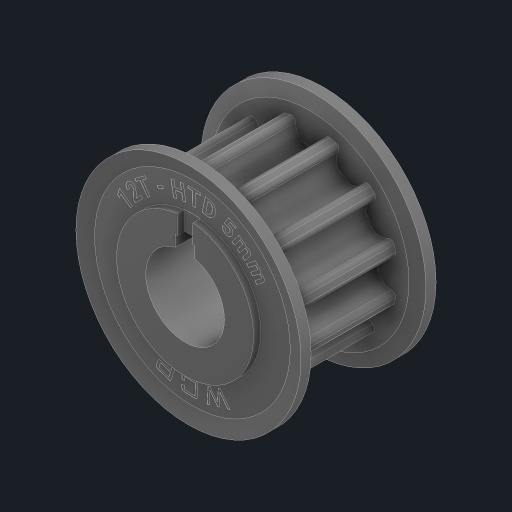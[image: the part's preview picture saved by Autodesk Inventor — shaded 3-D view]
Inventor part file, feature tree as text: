
AUTODESK INVENTOR PART (.ipt)
format: ipt  version: 2024.2 (Build 282272000, 272)  size: 535,552 bytes
history: native  units: in
note: dims shown in document units (in); Inventor stores cm internally (conversion verified against a paired STEP export)
features: other x2, mirror x1
ambient origin geometry x8: Origin, YZ Plane, XZ Plane, XY Plane, X Axis, Y Axis, Z Axis, Center Point
bodies: Solid1 (feature_tree), Solid2 (feature_tree), Solid3 (feature_tree)
feature tree (3):
  mirror  "Mirror1"
  other  "Cut-Extrude2"
  other  "Cut-Extrude3"
